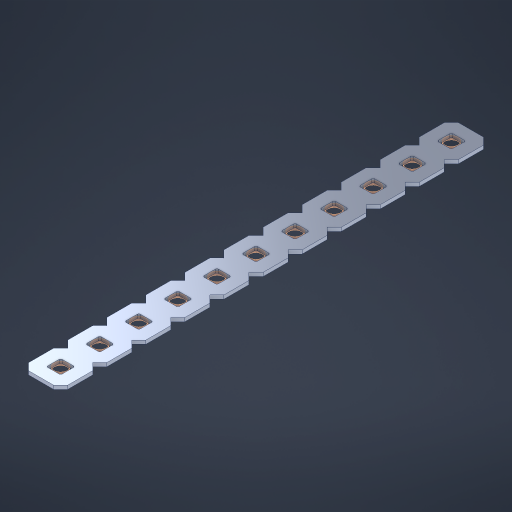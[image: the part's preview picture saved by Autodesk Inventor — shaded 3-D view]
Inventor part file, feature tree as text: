
AUTODESK INVENTOR PART (.ipt)
format: ipt  version: 2023 (Build 270158000, 158)  size: 401,920 bytes
history: native  units: in
note: dims shown in document units (in); Inventor stores cm internally (conversion verified against a paired STEP export)
features: other x12, extrude x10, sketch x2, pattern_linear x1
ambient origin geometry x8: Origin, YZ Plane, XZ Plane, XY Plane, X Axis, Y Axis, Z Axis, Center Point
bodies: Solid1 (feature_tree), Body (feature_tree)
feature tree (25):
  pattern_linear  "Rectangular Pattern1"  Spacing1=0.09in  [1 undecoded]
  sketch  "Sketch1"  dims[d1=0.5in]
  sketch  "Sketch2"  dims[d2=0.182in d3=0.09in d4=0.09in d5=0.09in d6=0.09in d7=0.09in d8=0.09in d9=0.09in d10=0.09in d11=0.02in d13=0.0in d14=0.172in d15=0.0625in d16=0.0in d19=0.5in d22=0.5in]
  other  "Srf1"
  other  "Srf126"
  other  "Srf127"
  other  "Srf128"
  other  "Srf129"
  other  "Srf130"
  other  "Srf131"
  other  "Srf250"
  other  "Srf251"
  other  "Srf252"
  other  "Srf253"
  other  "Circle"
  extrude  "ExtrusionSrf126"  Depth=0.09in
  extrude  "ExtrusionSrf127"  Depth=0.09in
  extrude  "ExtrusionSrf128"  Depth=0.09in
  extrude  "ExtrusionSrf129"  Depth=0.09in
  extrude  "ExtrusionSrf130"  Depth=0.09in
  extrude  "ExtrusionSrf131"  Depth=0.09in
  extrude  "ExtrusionSrf250"  Depth=0.09in
  extrude  "ExtrusionSrf251"  Depth=0.02in
  extrude  "ExtrusionSrf252"  TaperAngle=0.0deg  [1 undecoded]
  extrude  "ExtrusionSrf253"  Depth=0.5in
note: 2 required parameter values undecoded (feature->parameter linkage not recoverable at this tier; creation-order binding heuristic only, values carry confidence <= 0.55)
